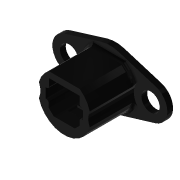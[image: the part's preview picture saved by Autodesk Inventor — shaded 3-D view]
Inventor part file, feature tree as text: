
AUTODESK INVENTOR PART (.ipt)
format: ipt  version: 2022 (Build 260153000, 153)  size: 164,352 bytes
history: native  units: in
note: dims shown in document units (in); Inventor stores cm internally (conversion verified against a paired STEP export)
features: reference x7, other x5, extrude x1, sketch x1
ambient origin geometry x8: Origin, YZ Plane, XZ Plane, XY Plane, X Axis, Y Axis, Z Axis, Center Point
bodies: Volumenkörper1 (feature_tree)
feature tree (14):
  other  "00_toslink_launcher_v3"
  extrude  "Extrusion1"  Depth=0.3543in TaperAngle=0.0deg
  sketch  "Skizze1"  dims[d0=0.2953in d1=0.3543in d2=0.0in]
  reference  "Referenz1"
  reference  "Referenz2"
  reference  "Referenz3"
  reference  "Referenz4"
  reference  "Referenz5"
  reference  "Referenz6"
  reference  "Referenz7"
  other  "MeshFeature1"
  other  "Spectroscope_v0.iam"
  other  "Spectrometer_pinholeholder_v0:1"
  other  "00_mk8_nozzle_0.4STEP:1"
